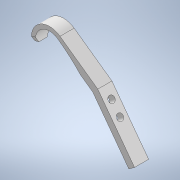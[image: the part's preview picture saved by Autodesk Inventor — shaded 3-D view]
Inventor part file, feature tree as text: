
AUTODESK INVENTOR PART (.ipt)
format: ipt  version: 2020 (Build 240168000, 168)  size: 217,088 bytes
history: native  units: mm
features: sketch x5, extrude x5, projected_geometry x4, thicken_offset x3, other x3, chamfer x2, fillet x2, reference x2, plane x1
ambient origin geometry x8: Origin, YZ Plane, XZ Plane, XY Plane, X Axis, Y Axis, Z Axis, Center Point
bodies: Solid1 (feature_tree)
feature tree (27):
  sketch  "Sketch1"  dims[d0=3.0mm d1=3.5mm]
  plane  "Work Plane1"
  extrude  "Extrusion1"  Depth=3.5mm
  extrude  "Extrusion3"  Depth=18.0mm
  thicken_offset  "Thicken1"
  extrude  "Extrusion4"  Depth=14.0mm
  extrude  "Extrusion5"  Depth=10.0mm
  chamfer  "Chamfer2"  Distance=10.0mm
  extrude  "Extrusion6"  Depth=20.0mm
  thicken_offset  "Thicken2"
  chamfer  "Chamfer3"  Distance=30.0mm
  thicken_offset  "Thicken3"
  fillet  "Fillet1"  Radius=18.849556mm
  fillet  "Fillet2"  Radius=3.5mm
  reference  "Reference1"
  reference  "Reference2"
  sketch  "Sketch3"  dims[d2=35.0mm d5=18.0mm]
  projected_geometry  "Projected Loop1"
  sketch  "Sketch4"  dims[d6=2.0mm d7=14.0mm]
  projected_geometry  "Projected Loop2"
  sketch  "Sketch5"  dims[d8=10.0mm d9=0.0mm d17=15.0mm d18=10.0mm d19=0.0mm]
  projected_geometry  "Projected Loop3"
  sketch  "Sketch6"  dims[d20=12.0mm d21=12.0mm d22=30.0mm d23=18.849556mm d24=3.5mm d25=10.0mm d26=0.0mm d27=6.981317mm d28=10.0mm d29=0.0mm d30=1.5mm d31=2.0mm d32=60.0deg d33=6.0mm d34=7.0mm d35=3.2mm d36=3.2mm d37=10.0mm d38=0.0mm d39=13.0mm d40=13.0mm d41=2.0mm d42=2.0mm d43=60.0deg d44=0.5mm d45=0.5mm d46=8.0mm d47=20.0mm]
  projected_geometry  "Projected Loop4"
  parser-record x1  (decoder bookkeeping rows leaked as tree rows — omitted from the tree; the rows remain in map.json)
  other  "leg_1.iam"
  other  "leg_link_1:1"
note: 1 file-system path scrubbed to <path> (originals preserved in map.json)
